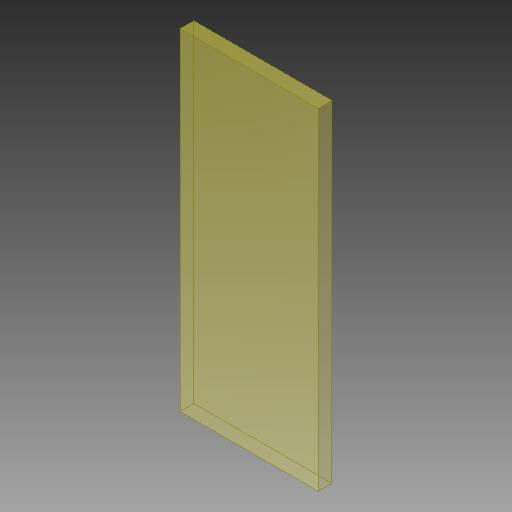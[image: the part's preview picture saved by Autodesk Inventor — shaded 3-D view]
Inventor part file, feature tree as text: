
AUTODESK INVENTOR PART (.ipt)
format: ipt  version: 2018.1 (Build 221171000, 171)  size: 92,672 bytes
history: native  units: mm
features: other x1, extrude x1, sketch x1
ambient origin geometry x8: Origin, YZ Plane, XZ Plane, XY Plane, X Axis, Y Axis, Z Axis, Center Point
bodies: Solid1 (feature_tree)
feature tree (3):
  parser-record x1  (decoder bookkeeping rows leaked as tree rows — omitted from the tree; the rows remain in map.json)
  extrude  "Extrusion1"  Depth=120.0mm
  sketch  "Sketch1"  dims[d0=50.0mm d1=120.0mm d2=5.0mm d3=0.0mm]
note: 1 file-system path scrubbed to <path> (originals preserved in map.json)
